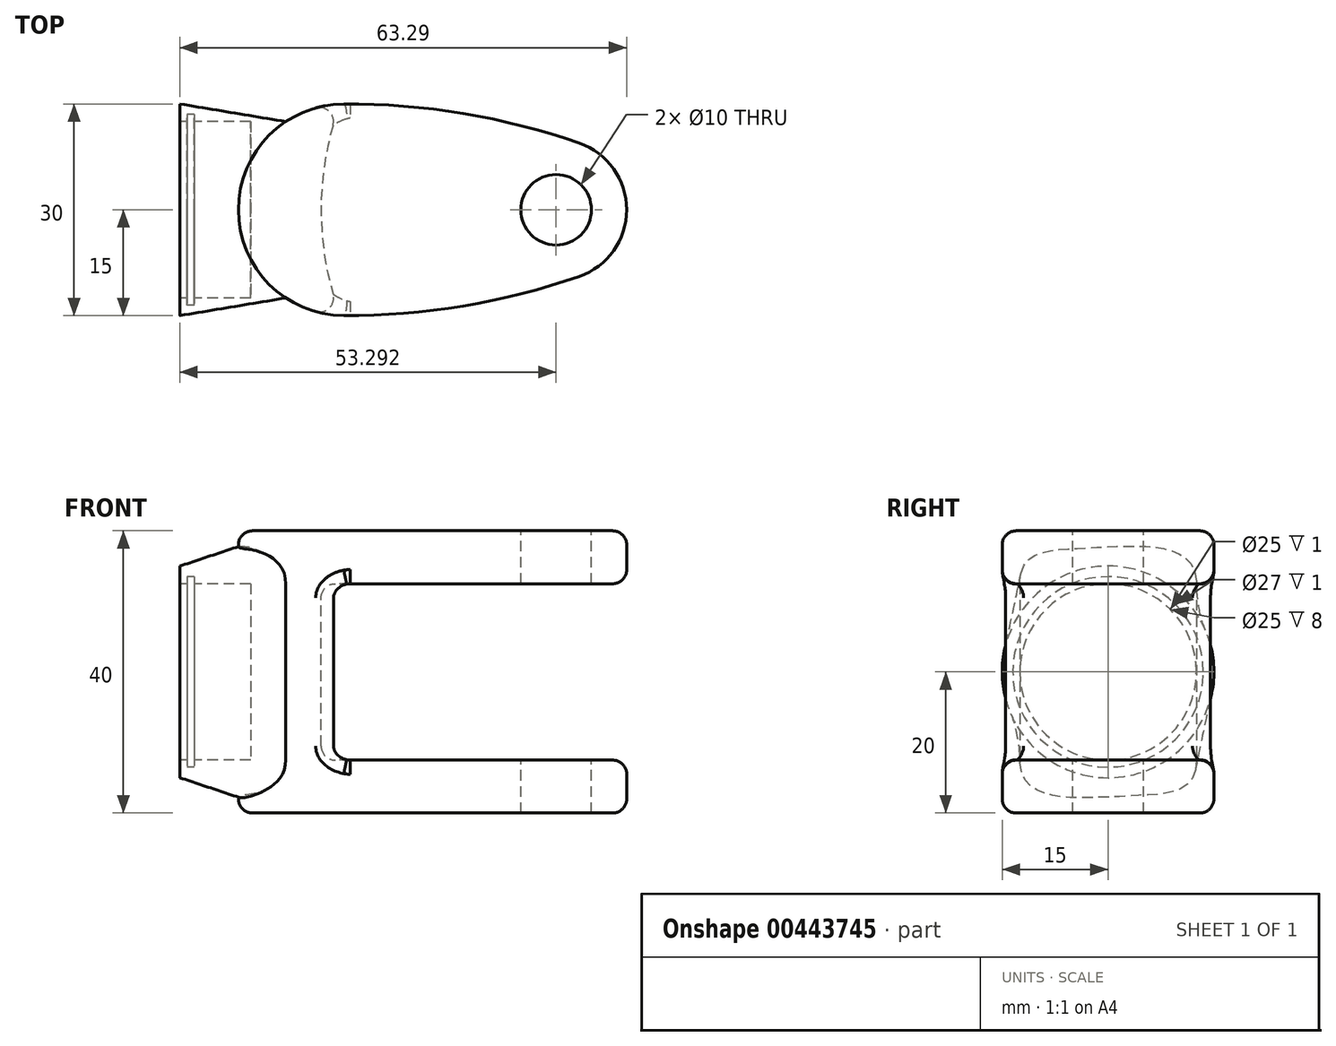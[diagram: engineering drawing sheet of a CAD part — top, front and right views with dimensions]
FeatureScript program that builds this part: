
annotation { "Feature Type Name" : "Feature", "Feature Type Description" : "" }
export const myFeature = defineFeature(function(context is Context, id is Id, definition is map)
    precondition{}
    {
        {
            var Q0;
            Q0=qCreatedBy(makeId("Right.planeOp"),FACE);
            var sketch = newSketch(context, id + "F0", { "sketchPlane" : qUnion([Q0])});
            skCircle(sketch, "E0", {"center": v(0, 0) * mm, "radius": 15 * mm});
            skSolve(sketch);
        }
        {
            var Q0;
            Q0=qCreatedBy(makeId("Right.planeOp"),FACE);
            cPlane(context, id + "F1", {"entities" : qUnion([Q0]), "cplaneType" : CPlaneType.OFFSET, "offset" : 15 * mm, "width" : 150 * mm, "height" : 150 * mm});
        }
        {
            var Q0;
            Q0=qCreatedBy(id+"F1.planeOp",FACE);
            var sketch = newSketch(context, id + "F2", { "sketchPlane" : qUnion([Q0])});
            skLineSegment(sketch, "E1.bottom", {"start": v(5, 20) * mm, "end": v(-5, 20) * mm});
            skLineSegment(sketch, "E1.top", {"start": v(5, -20) * mm, "end": v(-5, -20) * mm});
            skLineSegment(sketch, "E1.left", {"start": v(12.5, 12.5) * mm, "end": v(12.5, -12.5) * mm});
            skLineSegment(sketch, "E1.right", {"start": v(-12.5, 12.5) * mm, "end": v(-12.5, -12.5) * mm});
            skPoint(sketch, "E1.middle", {"position": v(0, 0) * mm});
            skPoint(sketch, "E2.visualSharp", {"position": v(-12.5, 20) * mm});
            skArc(sketch, "E2.filletArc", {"start": v(-5, 20) * mm, "mid": v(-10.3, 17.8) * mm, "end": v(-12.5, 12.5) * mm});
            skPoint(sketch, "E3.visualSharp", {"position": v(12.5, 20) * mm});
            skArc(sketch, "E3.filletArc", {"start": v(12.5, 12.5) * mm, "mid": v(10.3, 17.8) * mm, "end": v(5, 20) * mm});
            skPoint(sketch, "E4.visualSharp", {"position": v(12.5, -20) * mm});
            skArc(sketch, "E4.filletArc", {"start": v(5, -20) * mm, "mid": v(10.3, -17.8) * mm, "end": v(12.5, -12.5) * mm});
            skPoint(sketch, "E5.visualSharp", {"position": v(-12.5, -20) * mm});
            skArc(sketch, "E5.filletArc", {"start": v(-12.5, -12.5) * mm, "mid": v(-10.3, -17.8) * mm, "end": v(-5, -20) * mm});
            skSolve(sketch);
        }
        {
            var Q0;
            Q0=makeQuery(id+"F2.imprint","IMPRINT",FACE,{"disambiguationData":[TD([[makeQuery(id+"F2.imprint","IMPRINT",EDGE,{"derivedFrom":sQuery(id+"F2.wireOp",EDGE,"E1.bottom")}),1.0]])]});
            var Q1;
            Q1=makeQuery(id+"F0.imprint","IMPRINT",FACE,{"disambiguationData":[TD([[makeQuery(id+"F0.imprint","IMPRINT",EDGE,{"derivedFrom":sQuery(id+"F0.wireOp",EDGE,"E0")}),1.0]])]});
            loft(context, id + "F3", {"sheetProfilesArray" : [{ "sheetProfileEntities" : qUnion([Q0]) }, { "sheetProfileEntities" : qUnion([Q1]) }]});
        }
        {
            var Q0;
            Q0=qCreatedBy(makeId("Top.planeOp"),FACE);
            var sketch = newSketch(context, id + "F4", { "sketchPlane" : qUnion([Q0])});
            skArc(sketch, "E6", {"start": v(23.22, 15) * mm, "mid": v(8.3, 0) * mm, "end": v(23.22, -15) * mm});
            skArc(sketch, "E7", {"start": v(56.58, -9.44) * mm, "mid": v(63.3, 0) * mm, "end": v(56.58, 9.44) * mm});
            skArc(sketch, "E8", {"start": v(23.22, -15) * mm, "mid": v(40.13, -13.64) * mm, "end": v(56.58, -9.44) * mm});
            skArc(sketch, "E9", {"start": v(56.58, 9.44) * mm, "mid": v(40.13, 13.64) * mm, "end": v(23.22, 15) * mm});
            skSolve(sketch);
        }
        {
            var Q0;
            Q0 = qSketchRegion(id + "F4", true);
            extrude(context, id + "F5", {"entities" : qUnion([Q0]), "operationType" : NewBodyOperationType.ADD, "endBound" : BoundingType.SYMMETRIC, "depth" : 40 * mm});
        }
        {
            var Q0;
            Q0=qCreatedBy(makeId("Front.planeOp"),FACE);
            var sketch = newSketch(context, id + "F6", { "sketchPlane" : qUnion([Q0])});
            skLineSegment(sketch, "E10", {"start": v(63.3, 12.5) * mm, "end": v(20, 12.5) * mm});
            skLineSegment(sketch, "E11", {"start": v(20, 12.5) * mm, "end": v(20, -12.5) * mm});
            skLineSegment(sketch, "E12", {"start": v(20, -12.5) * mm, "end": v(63.3, -12.5) * mm});
            skLineSegment(sketch, "E13", {"start": v(63.3, -12.5) * mm, "end": v(63.3, 12.5) * mm});
            skSolve(sketch);
        }
        {
            var Q0;
            Q0 = qSketchRegion(id + "F6", true);
            var Q1;
            Q1=sQuery(id+"F6.wireOp",EDGE,"E13");
            revolve(context, id + "F7", {"operationType" : NewBodyOperationType.REMOVE, "entities" : qUnion([Q0]), "axis" : qUnion([Q1]), "revolveType" : RevolveType.FULL, "oppositeDirection" : true});
        }
        {
            var Q0;
            Q0=makeQuery(id+"F3.opLoft","CAP_FACE",FACE,{"disambiguationData":[OSD([makeQuery(id+"F0.imprint","IMPRINT",FACE,{"disambiguationData":[TD([[makeQuery(id+"F0.imprint","IMPRINT",EDGE,{"derivedFrom":sQuery(id+"F0.wireOp",EDGE,"E0")}),1.0]])]})])],"isStart":true});
            var sketch = newSketch(context, id + "F8", { "sketchPlane" : qUnion([Q0])});
            skCircle(sketch, "E14", {"center": v(0, 0) * mm, "radius": 12.5 * mm});
            skSolve(sketch);
        }
        {
            var Q0;
            Q0 = qSketchRegion(id + "F8", true);
            extrude(context, id + "F9", {"entities" : qUnion([Q0]), "operationType" : NewBodyOperationType.REMOVE, "oppositeDirection" : true, "depth" : 10 * mm});
        }
        {
            var Q0;
            Q0=makeQuery(id+"F3.opLoft","CAP_FACE",FACE,{"disambiguationData":[OSD([makeQuery(id+"F0.imprint","IMPRINT",FACE,{"disambiguationData":[TD([[makeQuery(id+"F0.imprint","IMPRINT",EDGE,{"derivedFrom":sQuery(id+"F0.wireOp",EDGE,"E0")}),1.0]])]})])],"isStart":true});
            cPlane(context, id + "F10", {"entities" : qUnion([Q0]), "cplaneType" : CPlaneType.OFFSET, "offset" : 1 * mm, "oppositeDirection" : true, "width" : 150 * mm, "height" : 150 * mm});
        }
        {
            var Q0;
            Q0=makeQuery(id+"F5.opExtrude","CAP_FACE",FACE,{"disambiguationData":[OSD([sQuery(id+"F4.wireOp",EDGE,"E6"),sQuery(id+"F4.wireOp",EDGE,"E7"),sQuery(id+"F4.wireOp",EDGE,"E8"),sQuery(id+"F4.wireOp",EDGE,"E9")])],"isStart":false});
            var sketch = newSketch(context, id + "F11", { "sketchPlane" : qUnion([Q0])});
            skCircle(sketch, "E15", {"center": v(53.3, 0) * mm, "radius": 5 * mm});
            skSolve(sketch);
        }
        {
            var Q0;
            Q0 = qSketchRegion(id + "F11", true);
            extrude(context, id + "F12", {"entities" : qUnion([Q0]), "operationType" : NewBodyOperationType.REMOVE, "endBound" : BoundingType.THROUGH_ALL, "oppositeDirection" : true, "depth" : 25 * mm});
        }
        {
            var Q0;
            Q0=makeQuery(id+"F7.boolean.opBoolean","COPY",EDGE,{"derivedFrom":makeQuery(id+"F7.opRevolve","SWEPT_EDGE",EDGE,{"disambiguationData":[OSD([sQuery(id+"F6.wireOp",EDGE,"E10"),sQuery(id+"F6.wireOp",EDGE,"E11")])]})});
            var Q1;
            Q1=makeQuery(id+"F7.boolean.opBoolean","COPY",EDGE,{"derivedFrom":makeQuery(id+"F7.opRevolve","SWEPT_EDGE",EDGE,{"disambiguationData":[OSD([sQuery(id+"F6.wireOp",EDGE,"E11"),sQuery(id+"F6.wireOp",EDGE,"E12")])]})});
            fillet(context, id + "F13", {"entities" : qUnion([Q0, Q1]), "radius" : 2 * mm, "tangentPropagation" : true, "allowEdgeOverflow" : false});
        }
        {
            var Q0;
            Q0=makeQuery(id+"F5.opExtrude","CAP_EDGE",EDGE,{"disambiguationData":[OSD([sQuery(id+"F4.wireOp",EDGE,"E8")])],"isStart":true});
            var Q1;
            Q1=makeQuery(id+"F7.boolean.opBoolean","INTERSECT",EDGE,{"derivedFrom":[makeQuery(id+"F5.opExtrude","SWEPT_FACE",FACE,{"disambiguationData":[OSD([sQuery(id+"F4.wireOp",EDGE,"E7")])]}),makeQuery(id+"F7.opRevolve","SWEPT_FACE",FACE,{"disambiguationData":[OSD([sQuery(id+"F6.wireOp",EDGE,"E12")])]})]});
            var Q2;
            Q2=makeQuery(id+"F7.boolean.opBoolean","INTERSECT",EDGE,{"derivedFrom":[makeQuery(id+"F5.opExtrude","SWEPT_FACE",FACE,{"disambiguationData":[OSD([sQuery(id+"F4.wireOp",EDGE,"E8")])]}),makeQuery(id+"F7.opRevolve","SWEPT_FACE",FACE,{"disambiguationData":[OSD([sQuery(id+"F6.wireOp",EDGE,"E12")])]})]});
            var Q3;
            Q3=makeQuery(id+"F7.boolean.opBoolean","INTERSECT",EDGE,{"derivedFrom":[makeQuery(id+"F5.opExtrude","SWEPT_FACE",FACE,{"disambiguationData":[OSD([sQuery(id+"F4.wireOp",EDGE,"E8")])]}),makeQuery(id+"F7.opRevolve","SWEPT_FACE",FACE,{"disambiguationData":[OSD([sQuery(id+"F6.wireOp",EDGE,"E10")])]})]});
            var Q4;
            Q4=makeQuery(id+"F5.opExtrude","CAP_EDGE",EDGE,{"disambiguationData":[OSD([sQuery(id+"F4.wireOp",EDGE,"E7")])],"isStart":false});
            var Q5;
            Q5=makeQuery(id+"F5.opExtrude","CAP_EDGE",EDGE,{"disambiguationData":[OSD([sQuery(id+"F4.wireOp",EDGE,"E8")])],"isStart":false});
            fillet(context, id + "F14", {"entities" : qUnion([Q0, Q1, Q2, Q3, Q4, Q5]), "radius" : 2 * mm, "tangentPropagation" : true, "allowEdgeOverflow" : false});
        }
        {
            var Q0;
            Q0=qCreatedBy(id+"F10.planeOp",FACE);
            var sketch = newSketch(context, id + "F15", { "sketchPlane" : qUnion([Q0])});
            skCircle(sketch, "E16.0", {"center": v(0, 0) * mm, "radius": 12.5 * mm});
            skSolve(sketch);
        }
        {
            var Q0;
            Q0=makeQuery(id+"F15.imprint","IMPRINT",FACE,{"disambiguationData":[TD([[makeQuery(id+"F15.imprint","IMPRINT",EDGE,{"derivedFrom":sQuery(id+"F15.wireOp",EDGE,"E16.0")}),1.0]])]});
            var sketch = newSketch(context, id + "F16", { "sketchPlane" : qUnion([Q0])});
            skCircle(sketch, "E17.0", {"center": v(0, 0) * mm, "radius": 11.5 * mm});
            skCircle(sketch, "E18.0", {"center": v(0, 0) * mm, "radius": 13.5 * mm});
            skSolve(sketch);
        }
        {
            var Q0;
            Q0 = qSketchRegion(id + "F16", true);
            extrude(context, id + "F17", {"entities" : qUnion([Q0]), "operationType" : NewBodyOperationType.REMOVE, "oppositeDirection" : true, "depth" : 1 * mm});
        }
    });
